# Revit family: Murfor Compact E-35 Masonry Reinforcement
name_source: partatom
category: Specialty Equipment
revit_build: Autodesk Revit 2018 (Build: 20190510_1515(x64)
units: mm (PartAtom-declared; Revit-internal decimal feet)

## family parameters
Always vertical = Yes
Cut with Voids When Loaded = No
Part Type = Normal
Room Calculation Point = No
Round Connector Dimension = Use Diameter
Shared = No
Work Plane-Based = No

## types (1)
- Murfor Compact E-35
    Application = Murfor Compacyt E-35 is made from Austenitic Stainless steel (Molybdene - chrome - nickel alloy). This type of reinforcement has been specifically designed for exterior masonry (exposure class MX2, MX3 and MX4, xompliant wit Eurocode 6/EN 845/3).
    Datasheet = https://www.bekaert.com
    Description = Compact masonry reinforcement, steel chords on interwoven fibreglass roving
    Keynote = suitable for all mortar joints with thickness between 3mm and 12mm.
    Longtidinal Cord = 0.69 mm
    Manufacturer = Bekaert
    Material = Austenitic Stainless Steel
    Material Coating Reference EN845-3 = R1
    Pitch (long) - b = 7.5 mm  [stored 0.0246063 ft]
    Pitch (short) - a = 5 mm  [stored 0.0164042 ft]
    Steel Section Total = 4.83 mm
    Step c = 33 mm  [stored 0.108268 ft]
    Strain Agt = 2
    Thickness - e = 1.75 mm  [stored 0.00574147 ft]
    Type Comments = A mesh consisiting of 7 steel coeds
    Type Image = Murfor Compact E-35.PNG
    URL = https://www.bekaert.com
    Weight kg/ roll = 1.34kg per roll
    Width - w = 35 mm  [stored 0.114829 ft]
    Yield Strength - Mpa = 1300
    Youngs Modulus - Gpa = 150
    Z = 36.5 mm  [stored 0.119751 ft]

note: [stored X ft] marks values corroborated as IEEE doubles in the binary element streams (Revit-internal decimal feet)

## geometry (parser evidence)
native form markers: Blend x2, Sweep x13
no freeform markers — native parametric forms only
